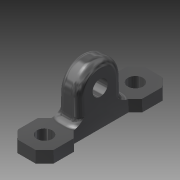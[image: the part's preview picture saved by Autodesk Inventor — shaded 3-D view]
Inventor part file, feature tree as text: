
AUTODESK INVENTOR PART (.ipt)
format: ipt  version: 2013 (Build 170138000, 138)  size: 254,976 bytes
history: native  units: in
note: dims shown in document units (in); Inventor stores cm internally (conversion verified against a paired STEP export)
features: sketch x5, extrude x4, fillet x2, hole x2, plane x1, other x1
ambient origin geometry x8: Origin, YZ Plane, XZ Plane, XY Plane, X Axis, Y Axis, Z Axis, Center Point
bodies: Solid1 (feature_tree)
feature tree (15):
  sketch  "Sketch1"  dims[d0=0.125in d1=-0.0137in d3=0.5in]
  extrude  "Extrusion1"  Depth=0.5in
  plane  "Work Plane1"
  extrude  "Extrusion2"  Depth=0.08in
  fillet  "Fillet2"  Radius=0.08in
  fillet  "Fillet3"  Radius=0.027in
  hole  "Hole1"  [1 undecoded]
  hole  "Hole2"  [1 undecoded]
  extrude  "Extrusion3"  [1 undecoded]
  sketch  "Sketch2"  dims[d4=0.125in d5=0.0in d7=0.08in d8=0.08in]
  sketch  "Sketch3"  dims[d9=0.167in d10=0.75in d11=0.375in d12=0.25in d13=0.5635in d14=1.0in d15=0.8108in]
  sketch  "Sketch4"  dims[d16=0.167in d17=0.75in d18=0.375in d19=0.25in d20=0.5635in d21=1.0in d22=0.8108in d23=0.027in d24=-0.0137in]
  sketch  "Sketch5"  dims[d25=1.0in d26=0.0in d27=0.0in]
  other  "Srf1"
  extrude  "ExtrusionSrf1"  [1 undecoded]
note: 4 required parameter values undecoded (feature->parameter linkage not recoverable at this tier; creation-order binding heuristic only, values carry confidence <= 0.55)
